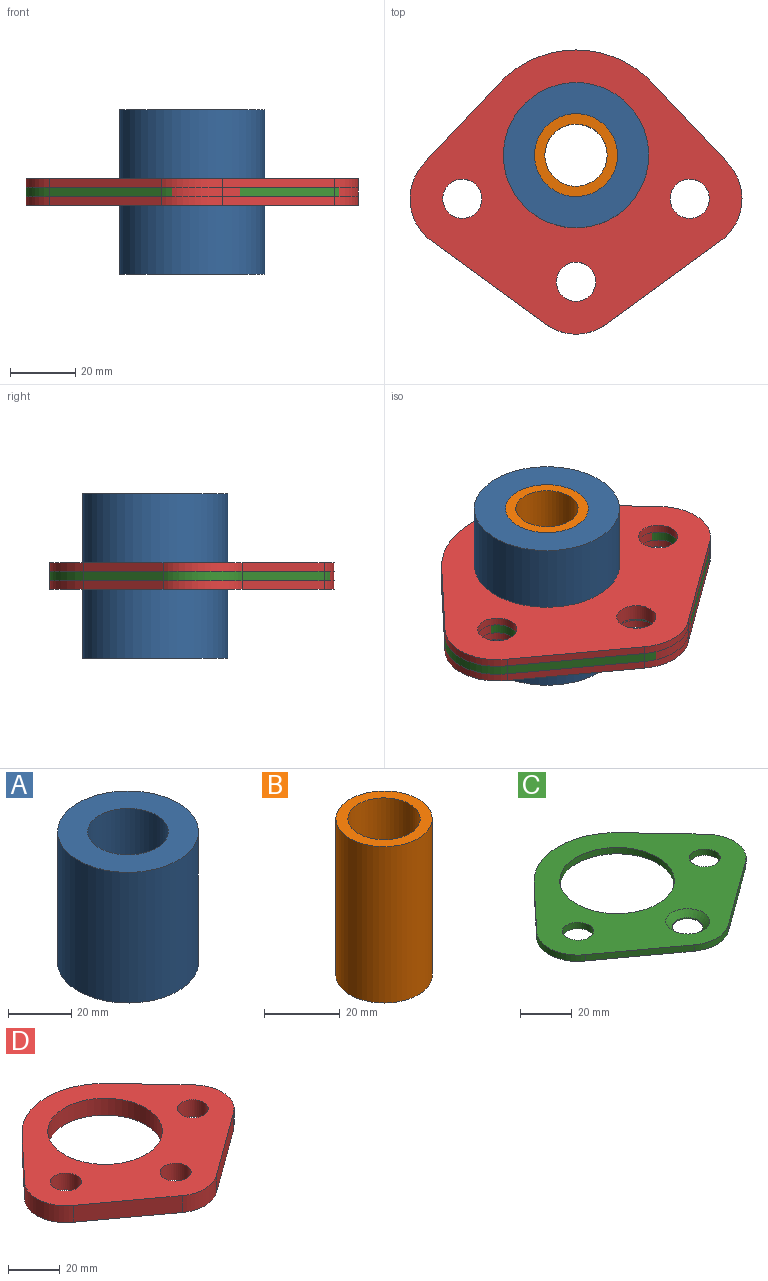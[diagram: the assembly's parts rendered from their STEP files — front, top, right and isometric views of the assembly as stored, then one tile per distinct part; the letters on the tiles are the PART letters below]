
ASSEMBLY  parts=4 mates=3
PART A: 4 faces, bbox 44.5x44.5x50.5 mm
  f0: cylinder r=12.7mm len=50.45mm, axis (0,0,1), area 4025.7mm2, adj f2,f3
  f1: cylinder r=22.23mm len=50.45mm, axis (0,0,1), area 7045mm2, adj f2,f3
  f2: plane 44.45x44.45mm, normal (0,0,-1), area 1045.1mm2, adj f0,f1
  f3: plane 44.45x44.45mm, normal (0,0,1), area 1045.1mm2, adj f0,f1
PART B: 4 faces, bbox 25.4x25.4x50.5 mm
  f0: cylinder r=9.53mm len=50.45mm, axis (0,0,1), area 3019.3mm2, adj f2,f3
  f1: cylinder r=12.7mm len=50.45mm, axis (0,0,1), area 4025.7mm2, adj f2,f3
  f2: plane 25.4x25.4mm, normal (0,0,-1), area 221.7mm2, adj f0,f1
  f3: plane 25.4x25.4mm, normal (0,0,1), area 221.7mm2, adj f0,f1
PART C: 15 faces, bbox 101.6x87x3 mm
  f0: plane 34.29x25.04mm, normal (0.59,-0.81,0), area 127.4mm2, adj f1,f10,f12,f13
  f1: cylinder r=16mm len=24.24mm, axis (0,0,-1), area 83.2mm2, adj f0,f2,f12,f13
  f2: plane 24.44x22.98mm, normal (0.73,0.68,0), area 100.6mm2, adj f1,f3,f12,f13
  f3: cylinder r=32.22mm len=46.96mm, axis (0,0,-1), area 157.8mm2, adj f2,f4,f12,f13
  f4: plane 24.44x22.98mm, normal (-0.73,0.68,0), area 100.6mm2, adj f3,f5,f12,f13
  f5: cylinder r=16mm len=24.24mm, axis (0,0,-1), area 83.2mm2, adj f4,f6,f12,f13
  f6: plane 34.29x25.04mm, normal (-0.59,-0.81,0), area 127.4mm2, adj f5,f10,f12,f13
  f7: cylinder r=6mm len=12mm, axis (0,0,-1), area 18.8mm2, adj f13,f14
  f8: cylinder r=6mm len=12mm, axis (0,0,-1), area 113.1mm2, adj f12,f13
  f9: cylinder r=22.23mm len=44.45mm, axis (0,0,-1), area 418.9mm2, adj f12,f13
  f10: cylinder r=16mm len=18.87mm, axis (0,0,-1), area 60.6mm2, adj f0,f6,f12,f13
  f11: cylinder r=6mm len=12mm, axis (0,0,-1), area 113.1mm2, adj f12,f13
  f12: plane 101.6x86.95mm, normal (0,0,1), area 3781.3mm2, adj f0,f1,f2,f3,f4,f5,f6,f8
  f13: plane 101.6x86.95mm, normal (0,0,-1), area 3895.1mm2, adj f0,f1,f2,f3,f4,f5,f6,f7
  f14: cone r=6mm half-angle=45deg, axis (0,0,1), area 161.1mm2, adj f7,f12
PART D: 14 faces, bbox 101.6x87x8 mm
  f0: plane 34.29x25.04mm, normal (0.59,-0.81,0), area 339.7mm2, adj f1,f10,f12,f13
  f1: cylinder r=16mm len=24.24mm, axis (0,0,-1), area 221.9mm2, adj f0,f2,f12,f13
  f2: plane 24.44x22.98mm, normal (0.73,0.68,0), area 268.4mm2, adj f1,f3,f12,f13
  f3: cylinder r=32.22mm len=46.96mm, axis (0,0,-1), area 420.8mm2, adj f2,f4,f12,f13
  f4: plane 24.44x22.98mm, normal (-0.73,0.68,0), area 268.4mm2, adj f3,f5,f12,f13
  f5: cylinder r=16mm len=24.24mm, axis (0,0,-1), area 221.9mm2, adj f4,f6,f12,f13
  f6: plane 34.29x25.04mm, normal (-0.59,-0.81,0), area 339.7mm2, adj f5,f10,f12,f13
  f7: cylinder r=6mm len=12mm, axis (0,0,-1), area 301.6mm2, adj f12,f13
  f8: cylinder r=6mm len=12mm, axis (0,0,-1), area 301.6mm2, adj f12,f13
  f9: cylinder r=22.23mm len=44.45mm, axis (0,0,-1), area 1117.2mm2, adj f12,f13
  f10: cylinder r=16mm len=18.87mm, axis (0,0,-1), area 161.5mm2, adj f0,f6,f12,f13
  f11: cylinder r=6mm len=12mm, axis (0,0,-1), area 301.6mm2, adj f12,f13
  f12: plane 101.6x86.95mm, normal (0,0,1), area 3895.1mm2, adj f0,f1,f2,f3,f4,f5,f6,f7
  f13: plane 101.6x86.95mm, normal (0,0,-1), area 3895.1mm2, adj f0,f1,f2,f3,f4,f5,f6,f7
PLACE A t=(0,0,20.73)mm
PLACE B rot(axis=(1,0,0),180deg) t=(0,0,-17.73)mm
PLACE C at identity
PLACE D t=(-37.44,-37.42,-2.5)mm
MATE fastened B.f1 <-> A.f1  axis (0,0,-1) through (0,0,-23.72)mm
MATE fastened A.f1 <-> D.f3  axis (0,0,1) through (0,0,1.5)mm
MATE fastened A.f1 <-> C.f9  axis (0,0,1) through (0,0,1.5)mm
